# Revit family: Urinal-Top_Spud-American_Standard- Pintbrook-6002_Series
name_source: partatom
category: Plumbing Fixtures
revit_build: Autodesk Revit 2014 (Build: 20130308_1515(x64)
units: mm (PartAtom-declared; Revit-internal decimal feet)

## types (4) — shared parameters
ADA Compliant = Yes
Assembly Code = D2010210
CW Connection = Yes
CWFU = 5
Cold Water Connection Diameter = 3/4"
Cold Water Connection Height = 11 1/2"
Cold Water Connection Radius = 3/8"
Cold Water Connection Width = 4 1/4"
Default Elevation = 24"
Finish = Vitreous China-American Standard-020-White
HW Connection = No
Height = 22 5/8"
Installation Type = Wall Hung
Length = 14 7/16"
Manufacturer = American Standard
Material = Vitreous China-American Standard-020-White
Price = Prices may vary. Please consult Manufacturer Representative for most up-to-date price list.
Product Documentation Link = https://www.americanstandard-us.com
Product Page URL = https://www.americanstandard-us.com
URL = http://www.americanstandard-us.com
Vent Connection = No
WFU = 5
Warranty Information = 1 Year Limated Warranty
Waste Connection = Yes
Waste Connection Diameter = 2"
Waste Connection Height = 5 1/2"
Waste Connection Radius = 1"
Width = 14 5/16"
zero-valued in all types: HWFU

## per-type parameters (varying)
| type | Description | Flush Rate | Flushvalve |
| 6002.501.020 | Pintbrook 0.5 gpf Urinal System with Manual Flush Valve | 0.5 gpf (1.9 Lpf) | Flush_Valve-Urinal-American_Standard-Exposed-Top_Spud-Manual_Series : 6045.051 |
| 6002.503.020 | Pintbrook 0.125 gpf Urinal System with Manual Flush Valve | 0.125 gpf (0.47 Lpf) | Flush_Valve-Urinal-American_Standard-Exposed-Top_Spud-Manual_Series : 6045.013 |
| 6002.505.020 | Pintbrook 0.5 gpf Urinal System with Selectronic Battery-Powered Flush Valve | 0.5 gpf (1.9 Lpf) | Flush_Valve-Urinal_Exposed-American_Standard-Selectronic_Series : 6063.051.002 |
| 6002.525.020 | Pintbrook 0.125 gpf Urinal System with Selectronic Battery-Powered Flush Valve | 0.125 gpf (0.47 Lpf) | Flush_Valve-Urinal_Exposed-American_Standard-Selectronic_Series : 6063.013.002 |

note: column(s) folded — value = type name in every type: Model

## geometry (parser evidence)
native form markers: Sweep x5
no freeform markers — native parametric forms only
